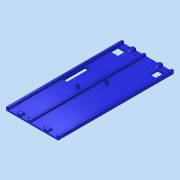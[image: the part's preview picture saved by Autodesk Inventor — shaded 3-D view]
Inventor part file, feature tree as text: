
AUTODESK INVENTOR PART (.ipt)
format: ipt  version: 2022 (Build 260153000, 153)  size: 249,856 bytes
history: native  units: in
note: dims shown in document units (in); Inventor stores cm internally (conversion verified against a paired STEP export)
features: extrude x10, sketch x10, chamfer x1
ambient origin geometry x8: Origin, YZ Plane, XZ Plane, XY Plane, X Axis, Y Axis, Z Axis, Center Point
bodies: Solid1 (feature_tree)
feature tree (21):
  extrude  "Extrusion1"  Depth=11.4173in
  extrude  "Extrusion2"  Depth=0.315in
  chamfer  "Chamfer1"  Distance=0.315in
  extrude  "Extrusion3"  Depth=0.0787in
  extrude  "Extrusion4"  Depth=0.1575in
  extrude  "Extrusion5"  Depth=0.2362in TaperAngle=0.0deg
  extrude  "Extrusion7"  Depth=0.7874in
  extrude  "Extrusion8"  Depth=0.1969in
  extrude  "Extrusion9"  Depth=0.1969in
  extrude  "Extrusion10"  Depth=0.1969in
  extrude  "Extrusion11"  Depth=0.1969in
  sketch  "Sketch1"  dims[d0=5.1181in d1=11.4173in]
  sketch  "Sketch2"  dims[d2=0.1181in d3=0.0in d4=0.315in]
  sketch  "Sketch3"  dims[d5=0.5512in]
  sketch  "Sketch4"  dims[d6=1.1811in d7=0.315in d8=0.0in]
  sketch  "Sketch5"  dims[d9=0.1969in d10=0.0787in d11=45.0deg d12=0.1378in]
  sketch  "Sketch7"  dims[d13=0.1575in d14=0.1575in]
  sketch  "Sketch8"  dims[d15=0.2362in d16=0.0in d17=0.2362in d18=0.0in]
  sketch  "Sketch9"  dims[d19=0.7874in d20=0.7874in]
  sketch  "Sketch10"  dims[d21=0.5906in d22=0.1969in]
  sketch  "Sketch11"  dims[d23=0.2362in d24=0.0in d39=2.7165in d40=3.3071in d41=1.5748in d42=1.5748in d43=0.315in d44=0.1575in d45=0.1575in d46=0.1772in d47=0.2362in d48=0.0in d49=0.315in d50=1.9291in d51=1.2598in d52=0.1772in d53=0.3937in d54=3.937in d55=2.1654in d56=0.2953in d57=0.2362in d58=0.0in d60=0.3937in d61=0.0984in d62=1.5748in d63=0.3937in d64=0.0in d65=0.1969in d66=0.1969in d67=0.0in d68=0.1969in d69=0.4528in d70=0.1969in d71=0.0in]
